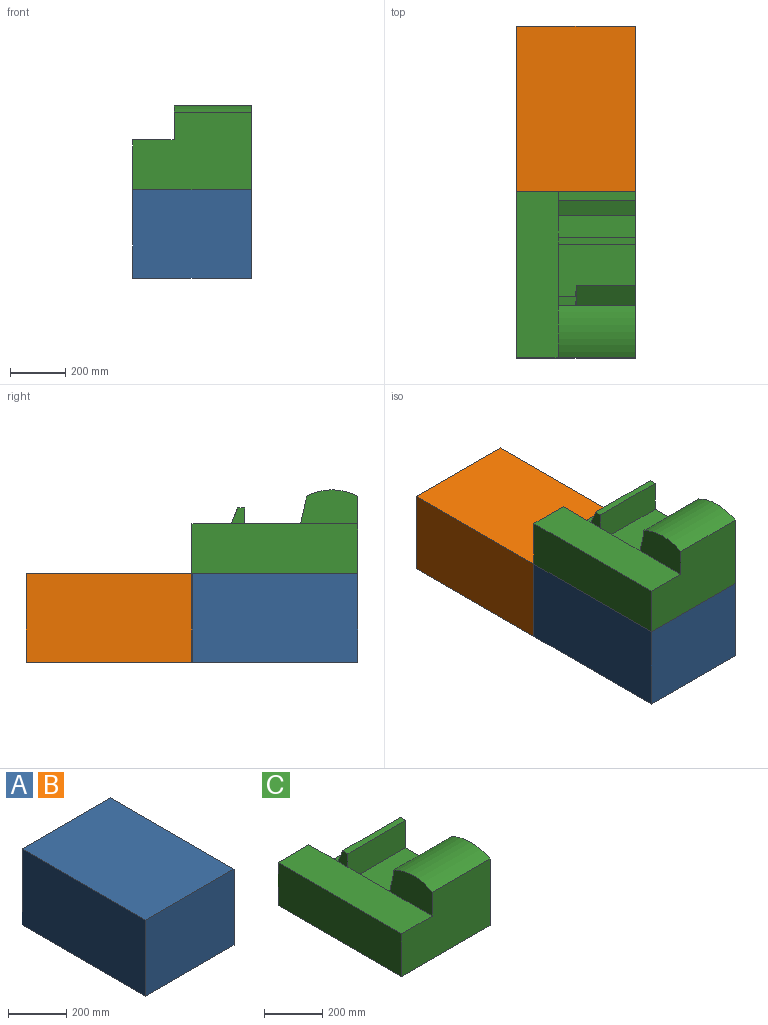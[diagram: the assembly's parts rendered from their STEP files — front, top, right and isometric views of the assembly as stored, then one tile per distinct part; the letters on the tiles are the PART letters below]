
ASSEMBLY  parts=3 mates=1
PART A: 50 faces, bbox 430x600x320 mm
  f0: cylinder r=50mm len=250mm, axis (-1,0,0), area 15989.4mm2, adj f1,f3,f10,f25
  f1: plane 197.8x120mm, normal (1,0,0), area 21678mm2, adj f0,f2,f3,f4,f5,f6,f7,f8
  f2: cylinder r=10mm len=250mm, axis (-1,0,0), area 3701.9mm2, adj f1,f3,f4,f25
  f3: plane 250x55.56mm, normal (0,-0.29,-0.96), area 14501.2mm2, adj f0,f1,f2,f25
  f4: plane 250x39.73mm, normal (0,0.93,-0.37), area 10701.9mm2, adj f1,f2,f5,f25
  f5: cylinder r=10mm len=250mm, axis (-1,0,0), area 954.3mm2, adj f1,f4,f6,f25
  f6: plane 250x138.07mm, normal (0,1,0), area 34517mm2, adj f1,f5,f7,f25
  f7: cylinder r=10mm len=250mm, axis (-1,0,0), area 3927mm2, adj f1,f6,f8,f25
  f8: plane 250x100mm, normal (0,0,1), area 25000mm2, adj f1,f7,f9,f25
  f9: cylinder r=10mm len=250mm, axis (-1,0,0), area 3927mm2, adj f1,f8,f10,f25
  f10: plane 250x122.81mm, normal (0,-1,0), area 30701.5mm2, adj f0,f1,f9,f25
  f11: cylinder r=50mm len=250mm, axis (-1,0,0), area 15989.4mm2, adj f12,f14,f21,f25
  f12: plane 197.8x120mm, normal (1,0,0), area 21678mm2, adj f11,f13,f14,f15,f16,f17,f18,f19
  f13: cylinder r=10mm len=250mm, axis (-1,0,0), area 3701.9mm2, adj f12,f14,f15,f25
  f14: plane 250x55.56mm, normal (0,-0.29,-0.96), area 14501.2mm2, adj f11,f12,f13,f25
  f15: plane 250x39.73mm, normal (0,0.93,-0.37), area 10701.9mm2, adj f12,f13,f16,f25
  f16: cylinder r=10mm len=250mm, axis (-1,0,0), area 954.3mm2, adj f12,f15,f17,f25
  f17: plane 250x138.07mm, normal (0,1,0), area 34517mm2, adj f12,f16,f18,f25
  f18: cylinder r=10mm len=250mm, axis (-1,0,0), area 3927mm2, adj f12,f17,f19,f25
  f19: plane 250x100mm, normal (0,0,1), area 25000mm2, adj f12,f18,f20,f25
  f20: cylinder r=10mm len=250mm, axis (-1,0,0), area 3927mm2, adj f12,f19,f21,f25
  f21: plane 250x122.81mm, normal (0,-1,0), area 30701.5mm2, adj f11,f12,f20,f25
  f22: plane 600x430mm, normal (0,0,1), area 258000mm2, adj f23,f25,f26,f27
  f23: plane 600x320mm, normal (-1,0,0), area 192000mm2, adj f22,f24,f26,f27
  f24: plane 600x430mm, normal (0,0,-1), area 258000mm2, adj f23,f25,f26,f27
  f25: plane 600x320mm, normal (1,0,0), area 105287.8mm2, adj f0,f2,f3,f4,f5,f6,f7,f8
  f26: plane 430x320mm, normal (0,-1,0), area 137600mm2, adj f22,f23,f24,f25
  f27: plane 430x320mm, normal (0,1,0), area 137600mm2, adj f22,f23,f24,f25
  f28: plane 250x138.07mm, normal (0,1,0), area 34517mm2, adj f25,f33,f36,f37
  f29: plane 250x39.73mm, normal (0,0.93,-0.37), area 10701.9mm2, adj f25,f33,f37,f38
  f30: plane 250x55.56mm, normal (0,-0.29,-0.96), area 14501.2mm2, adj f25,f33,f34,f38
  f31: plane 250x122.81mm, normal (0,-1,0), area 30701.5mm2, adj f25,f33,f34,f35
  f32: plane 250x100mm, normal (0,0,1), area 25000mm2, adj f25,f33,f35,f36
  f33: plane 197.8x120mm, normal (1,0,0), area 21678mm2, adj f28,f29,f30,f31,f32,f34,f35,f36
  f34: cylinder r=50mm len=250mm, axis (-1,0,0), area 15989.4mm2, adj f25,f30,f31,f33
  f35: cylinder r=10mm len=250mm, axis (-1,0,0), area 3927mm2, adj f25,f31,f32,f33
  f36: cylinder r=10mm len=250mm, axis (-1,0,0), area 3927mm2, adj f25,f28,f32,f33
  f37: cylinder r=10mm len=250mm, axis (-1,0,0), area 954.3mm2, adj f25,f28,f29,f33
  f38: cylinder r=10mm len=250mm, axis (-1,0,0), area 3701.9mm2, adj f25,f29,f30,f33
  f39: plane 250x122.81mm, normal (0,-1,0), area 30701.5mm2, adj f25,f40,f48,f49
  f40: cylinder r=10mm len=250mm, axis (-1,0,0), area 3927mm2, adj f25,f39,f41,f48
  f41: plane 250x100mm, normal (0,0,1), area 25000mm2, adj f25,f40,f42,f48
  f42: cylinder r=10mm len=250mm, axis (-1,0,0), area 3927mm2, adj f25,f41,f43,f48
  f43: plane 250x138.07mm, normal (0,1,0), area 34517mm2, adj f25,f42,f44,f48
  f44: cylinder r=10mm len=250mm, axis (-1,0,0), area 954.3mm2, adj f25,f43,f45,f48
  f45: plane 250x39.73mm, normal (0,0.93,-0.37), area 10701.9mm2, adj f25,f44,f47,f48
  f46: plane 250x55.56mm, normal (0,-0.29,-0.96), area 14501.2mm2, adj f25,f47,f48,f49
  f47: cylinder r=10mm len=250mm, axis (-1,0,0), area 3701.9mm2, adj f25,f45,f46,f48
  f48: plane 197.8x120mm, normal (1,0,0), area 21678mm2, adj f39,f40,f41,f42,f43,f44,f45,f46
  f49: cylinder r=50mm len=250mm, axis (-1,0,0), area 15989.4mm2, adj f25,f39,f46,f48
PART B: same geometry as A
PART C: 29 faces, bbox 430x600x303.3 mm
  f0: plane 202.69x57.24mm, normal (1,0,0), area 11237.9mm2, adj f16,f24,f25,f28
  f1: plane 215x95.26mm, normal (0,-0.55,0.84), area 24456.7mm2, adj f2,f13,f25,f27
  f2: plane 215x51.68mm, normal (0,0.34,0.94), area 11825mm2, adj f1,f3,f13,f27
  f3: plane 215x69.79mm, normal (0,0.94,-0.34), area 15968.2mm2, adj f2,f4,f13,f27
  f4: plane 215x21.15mm, normal (0,-0.34,-0.94), area 4839.2mm2, adj f3,f5,f13,f27
  f5: plane 215x14.1mm, normal (0,0.94,-0.34), area 3225mm2, adj f4,f6,f13,f27
  f6: plane 215x51.68mm, normal (0,0.34,0.94), area 11825mm2, adj f5,f7,f13,f27
  f7: plane 215x28.19mm, normal (0,0.94,-0.34), area 6450mm2, adj f6,f8,f13,f27
  f8: plane 215x91.89mm, normal (0,0.94,0.34), area 21014.7mm2, adj f7,f9,f13,f27
  f9: cylinder r=191.22mm len=215mm, axis (1,0,0), area 21841.7mm2, adj f8,f13,f26,f27
  f10: plane 57.76x47.9mm, normal (-1,0,0), area 2105.4mm2, adj f16,f22,f23,f24
  f11: plane 600x180mm, normal (-1,0,0), area 108000mm2, adj f12,f14,f15,f16
  f12: plane 600x430mm, normal (0,0,-1), area 258000mm2, adj f11,f13,f14,f15
  f13: plane 600x303.3mm, normal (1,0,0), area 87770.5mm2, adj f1,f2,f3,f4,f5,f6,f7,f8
  f14: plane 430x280mm, normal (0,-1,0), area 105400mm2, adj f11,f12,f13,f16,f17,f19
  f15: plane 430x180mm, normal (0,1,0), area 43800mm2, adj f11,f12,f13,f16,f18,f20
  f16: plane 600x150mm, normal (0,0,1), area 90000mm2, adj f0,f10,f11,f14,f15,f17,f18
  f17: plane 207.31x123.3mm, normal (-1,0,0), area 22580.3mm2, adj f14,f16,f19,f26,f28
  f18: plane 142.11x142.1mm, normal (1,0,0), area 14912.2mm2, adj f15,f16,f20,f21,f22
  f19: cylinder r=200mm len=280mm, axis (1,0,0), area 54600mm2, adj f13,f14,f17,f26
  f20: plane 280x30mm, normal (0,0,1), area 8400mm2, adj f13,f15,f18,f21
  f21: plane 280x55.78mm, normal (0,-0.37,0.93), area 16800mm2, adj f13,f18,f20,f22
  f22: plane 280x199.87mm, normal (0,0.93,0.37), area 60200mm2, adj f10,f13,f18,f21,f23
  f23: plane 280x25mm, normal (0,0,1), area 7000mm2, adj f10,f13,f22,f24
  f24: plane 280x115mm, normal (0,-1,0), area 32200mm2, adj f0,f10,f13,f23,f25
  f25: plane 280x190mm, normal (0,0,1), area 44600mm2, adj f0,f1,f13,f24,f27,f28
  f26: plane 280x10mm, normal (0,1,0), area 2800mm2, adj f9,f13,f17,f19,f28
  f27: plane 233.93x170mm, normal (1,0,0), area 18765.1mm2, adj f1,f2,f3,f4,f5,f6,f7,f8
  f28: plane 147.24x65mm, normal (0,0.98,0.22), area 9802.6mm2, adj f0,f17,f25,f26,f27
PLACE A t=(-114.37,1274.18,305.46)mm
PLACE B t=(-114.37,1874.18,305.46)mm
PLACE C t=(-114.37,1274.18,625.46)mm
MATE revolute C.f14 <-> A.f26  axis (0,-1,0) through (-329.37,674.18,625.46)mm
